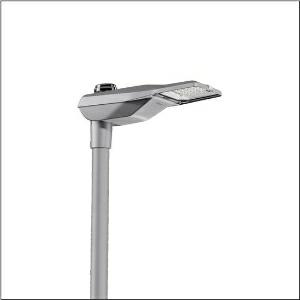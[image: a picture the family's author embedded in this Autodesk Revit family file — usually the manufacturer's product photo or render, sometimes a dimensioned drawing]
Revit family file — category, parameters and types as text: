
# Revit family: streetlight_sl_21_micro___st1_0a_5xe5d47n08db_8e26
name_source: partatom
category: Lighting Fixtures
units: mm (PartAtom-declared; Revit-internal decimal feet)

## family parameters
Cut with Voids When Loaded = No
Host = Face
Light Source = No
Part Type = Normal
Room Calculation Point = No
Round Connector Dimension = Use Diameter
Shared = No

## types (1)
- --- (1 x LED, 5320 lm, 39.1 W, 4000K)
    Apparent Load = 39 VA
    CIE Flux Codes = 37 72 97 100 100
    Color Rendering = 70
    Color Temperature = 4000K
    Default Elevation = 1800 mm
    Description = Streetlight SL 21 micro, mast luminaire, primary light control with lens, of PMMA, primary optical cover: cover, of toughened safety glass, transparent, light distribution: ST1.0a, light emission: direct distribution, primary light characteristic: asymmetric, installation type: post-top, LED, 3G 1.5mm², High Power LED, rated luminous flux: 5.320lm, luminous efficacy: 136lm/W, light colour: 740, colour temperature: 4000K, control gear: NEMA (7pin), control: overheat protection, pre-setting: linear dimming characteristic, constant luminous flux control, time-dependent luminous flux control, flexible luminous flux parameterisation, mains connection: 230..240V, AC, 50/60Hz, connection cable pre-assembled, cable length: 6,5m, wiring characteristics: H07RN-F, start of lifetime: 39W, end of service life: 41W, reduction: 18W, luminaire housing, of diecast aluminium (EN AC-44300), powder-coated, Siteco® metallic grey (DB 702S), corrosivity category C5 mid according to DIN EN ISO 12944, multi-level sealing system, sealing non-destructively replaceable, inclination adjustable: 0°, 5°, 10°, 15°, length: 528mm, width: 235mm, height: 110mm, spigot size: 76/60mm (post-top), mounting height: 4..8m, protection rating (complete): IP66, insulation class (complete): insulation class I (protective earthing), certification: CE, ENEC, ENEC+, VDE, impact resistance: IK10, permissible operating ambient temperature for outdoor applications: -40..+50°C, standard-compliant lighting for roads and squares, packaging unit: 1 piece

Light Distribution: ST1.0a
    Height = 110 mm
    Lamp = 1 x LED
    Lamp Light Flux = 5320 lm
    Lamp Power = 39.1 W
    Lamp count = 1
    Length = 528 mm
    Luminous efficacy = 136 lm/W
    Manufacturer = Siteco
    ModVariant = No
    Model = 5XE5D47N08DB
    Number of Poles = 1
    OnlyDefault = Yes
    Power Factor = 1
    Product Name = Streetlight SL 21 micro | ST1.0a
    Product group = mast luminaire | pylon top
    ProductGroupID = 6100
    Protection Class = Protection class I
    Protection Degree = IP 66
    RLX_Detail_Level = 1
    RLX_Emergency_Light_Flux = 0 lm
    RLX_Emergency_Type = 0
    RLX_Emergency_Type_DB = No
    RlxData = <blob elided: 98845 chars, md5=ea0b908c>
    Socket = socket
    Standby Power = 0 W
    System Light Flux = 5320 lm
    System Power = 39 W
    Type Comments = factory setting: luminous flux: 100 % | dim-lin: 254 | 765 mA
    Type Image = l_1294375.jpg
    URL = http://relux.com
    VarID = @adj_157955
    Voltage = 0 V
    Weight = 0.00 kg
    Width = 235 mm

## geometry (parser evidence)
native form markers: Blend x4, Sweep x10
no freeform markers — native parametric forms only
